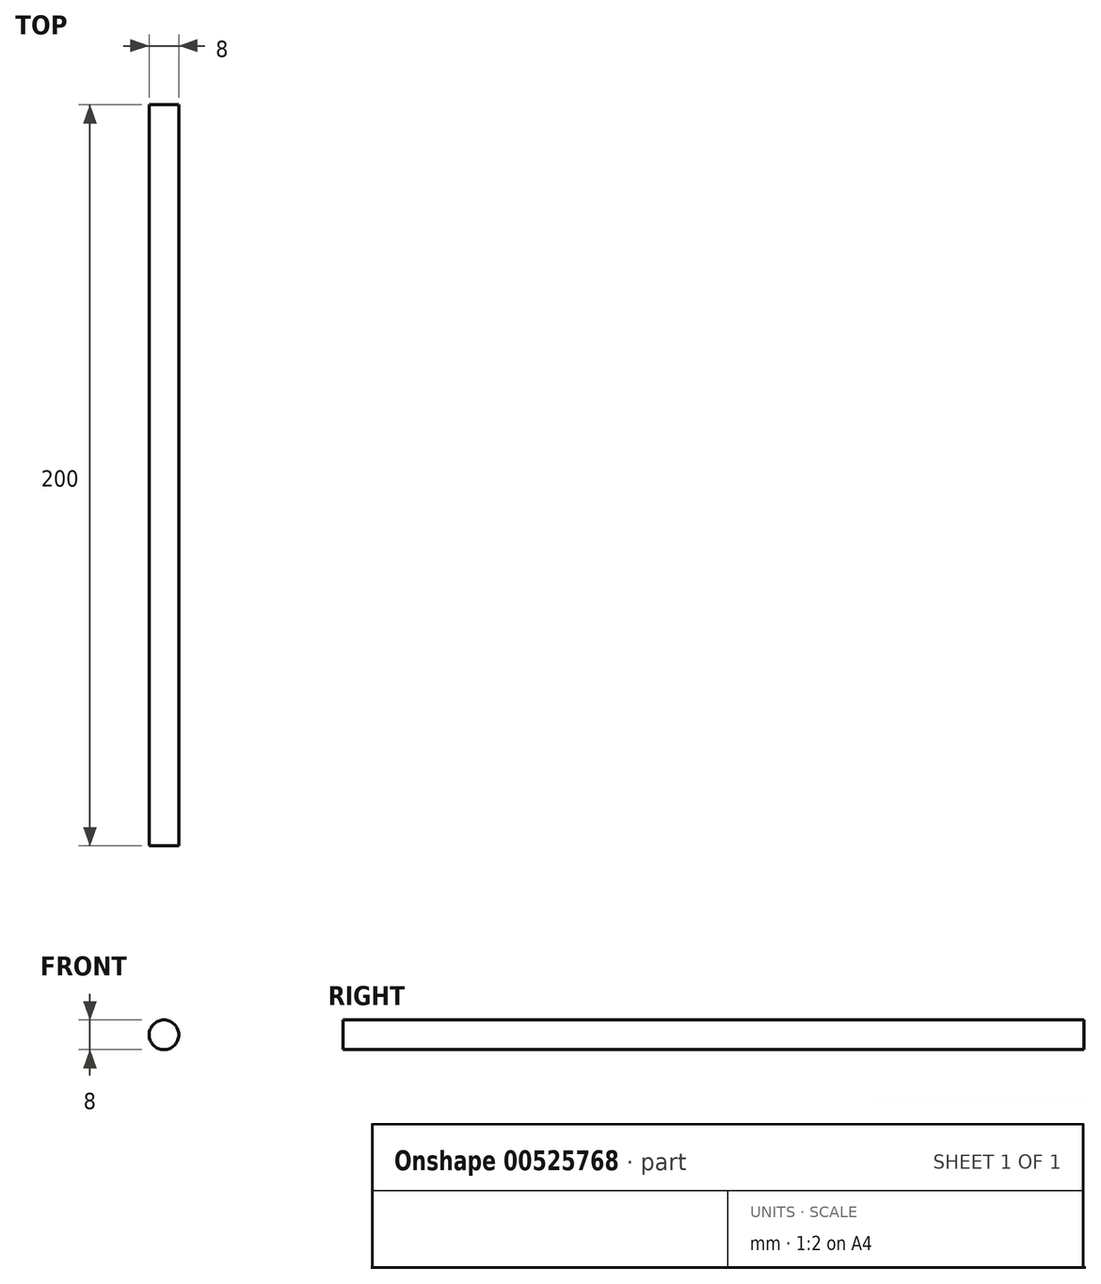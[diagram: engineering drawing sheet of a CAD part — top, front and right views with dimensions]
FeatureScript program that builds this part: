
annotation { "Feature Type Name" : "Feature", "Feature Type Description" : "" }
export const myFeature = defineFeature(function(context is Context, id is Id, definition is map)
    precondition{}
    {
        {
            var Q0;
            Q0=qCreatedBy(makeId("Front.planeOp"),FACE);
            var sketch = newSketch(context, id + "F0", { "sketchPlane" : qUnion([Q0])});
            skCircle(sketch, "E0", {"center": v(13.4, 26.47) * mm, "radius": 4 * mm});
            skSolve(sketch);
        }
        {
            var Q0;
            Q0 = qSketchRegion(id + "F0", true);
            extrude(context, id + "F1", {"entities" : qUnion([Q0]), "depth" : 200 * mm, "offsetDistance" : 25 * mm});
        }
    });
